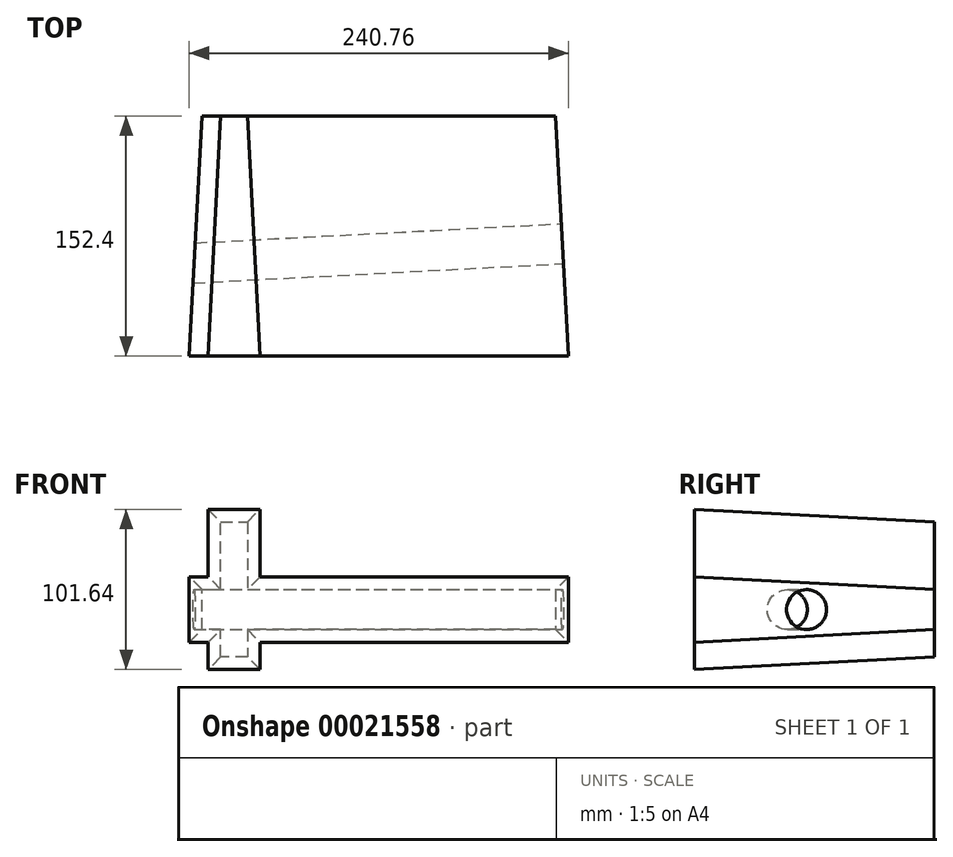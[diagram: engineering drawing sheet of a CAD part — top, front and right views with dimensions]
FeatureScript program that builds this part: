
annotation { "Feature Type Name" : "Feature", "Feature Type Description" : "" }
export const myFeature = defineFeature(function(context is Context, id is Id, definition is map)
    precondition{}
    {
        {
            var Q0;
            Q0=qCreatedBy(makeId("Front.planeOp"),FACE);
            var sketch = newSketch(context, id + "F0", { "sketchPlane" : qUnion([Q0])});
            skLineSegment(sketch, "E0.rect.bottom", {"start": v(-112.4, 12.76) * mm, "end": v(-100.4, 12.76) * mm});
            skLineSegment(sketch, "E0.rect.top", {"start": v(-112.4, -12.76) * mm, "end": v(-100.4, -12.76) * mm});
            skLineSegment(sketch, "E0.rect.left", {"start": v(-112.4, 12.76) * mm, "end": v(-112.4, -12.76) * mm});
            skLineSegment(sketch, "E0.rect.right", {"start": v(112.4, 12.76) * mm, "end": v(112.4, -12.76) * mm});
            skPoint(sketch, "E0.rect.middle", {"position": v(0, 0) * mm});
            skLineSegment(sketch, "E1.rect.bottom", {"start": v(-83.42, 55.6) * mm, "end": v(-100.4, 55.6) * mm});
            skLineSegment(sketch, "E1.rect.top", {"start": v(-83.42, -30.07) * mm, "end": v(-100.4, -30.07) * mm});
            skLineSegment(sketch, "E1.rect.left", {"start": v(-83.42, 55.6) * mm, "end": v(-83.42, 12.76) * mm});
            skLineSegment(sketch, "E1.rect.right", {"start": v(-100.4, 55.6) * mm, "end": v(-100.4, 12.76) * mm});
            skPoint(sketch, "E1.rect.middle", {"position": v(-91.91, 12.76) * mm});
            skLineSegment(sketch, "E2.trimOffspring", {"start": v(-83.42, 12.76) * mm, "end": v(112.4, 12.76) * mm});
            skLineSegment(sketch, "E3.trimOffspring", {"start": v(-100.4, -12.76) * mm, "end": v(-100.4, -30.07) * mm});
            skLineSegment(sketch, "E4.trimOffspring", {"start": v(-83.42, -12.76) * mm, "end": v(-83.42, -30.07) * mm});
            skLineSegment(sketch, "E5.trimOffspring", {"start": v(-83.42, -12.76) * mm, "end": v(112.4, -12.76) * mm});
            skLineSegment(sketch, "E6", {"start": v(-122.88, -45.21) * mm, "end": v(142.36, -45.21) * mm, "construction": true});
            skSolve(sketch);
        }
        {
            var Q0;
            Q0 = qSketchRegion(id + "F0", true);
            extrude(context, id + "F1", {"entities" : qUnion([Q0]), "depth" : 152.4 * mm, "hasDraft" : true, "draftAngle" : 3 * degree});
        }
        {
            var Q0;
            Q0=makeQuery(id+"F1.opExtrude","SWEPT_FACE",FACE,{"disambiguationData":[OSD([sQuery(id+"F0.wireOp",EDGE,"E0.rect.right")])]});
            var sketch = newSketch(context, id + "F2", { "sketchPlane" : qUnion([Q0])});
            skCircle(sketch, "E7", {"center": v(-87.07, 0) * mm, "radius": 12.7 * mm});
            skSolve(sketch);
        }
        {
            var Q0;
            Q0 = qSketchRegion(id + "F2", true);
            extrude(context, id + "F3", {"entities" : qUnion([Q0]), "operationType" : NewBodyOperationType.REMOVE, "oppositeDirection" : true, "depth" : 328.4 * mm});
        }
    });
